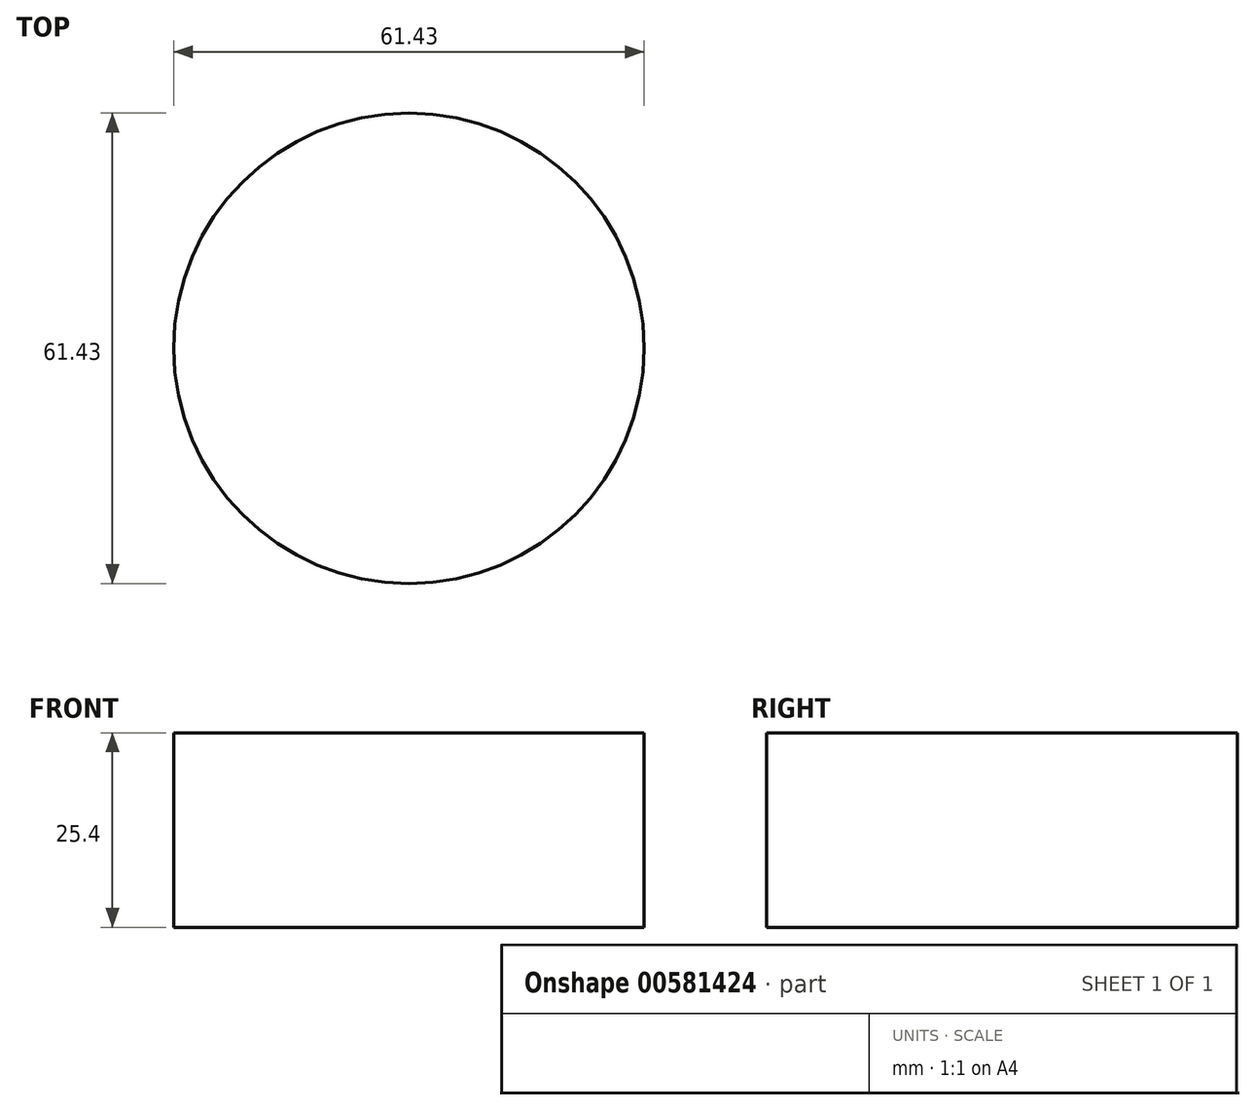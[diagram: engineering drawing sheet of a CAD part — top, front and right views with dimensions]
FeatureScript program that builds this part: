
annotation { "Feature Type Name" : "Feature", "Feature Type Description" : "" }
export const myFeature = defineFeature(function(context is Context, id is Id, definition is map)
    precondition{}
    {
        {
            var Q0;
            Q0=qCreatedBy(makeId("Top.planeOp"),FACE);
            var sketch = newSketch(context, id + "F0", { "sketchPlane" : qUnion([Q0])});
            skCircle(sketch, "E0", {"center": v(0.94, 0.2) * mm, "radius": 30.71 * mm});
            skSolve(sketch);
        }
        {
            var Q0;
            Q0=makeQuery(id+"F0.imprint","IMPRINT",FACE,{"disambiguationData":[TD([[makeQuery(id+"F0.imprint","IMPRINT",EDGE,{"derivedFrom":sQuery(id+"F0.wireOp",EDGE,"E0")}),1.0]])]});
            extrude(context, id + "F1", {"entities" : qUnion([Q0]), "depth" : 25.4 * mm, "offsetDistance" : 25.4 * mm});
        }
    });
